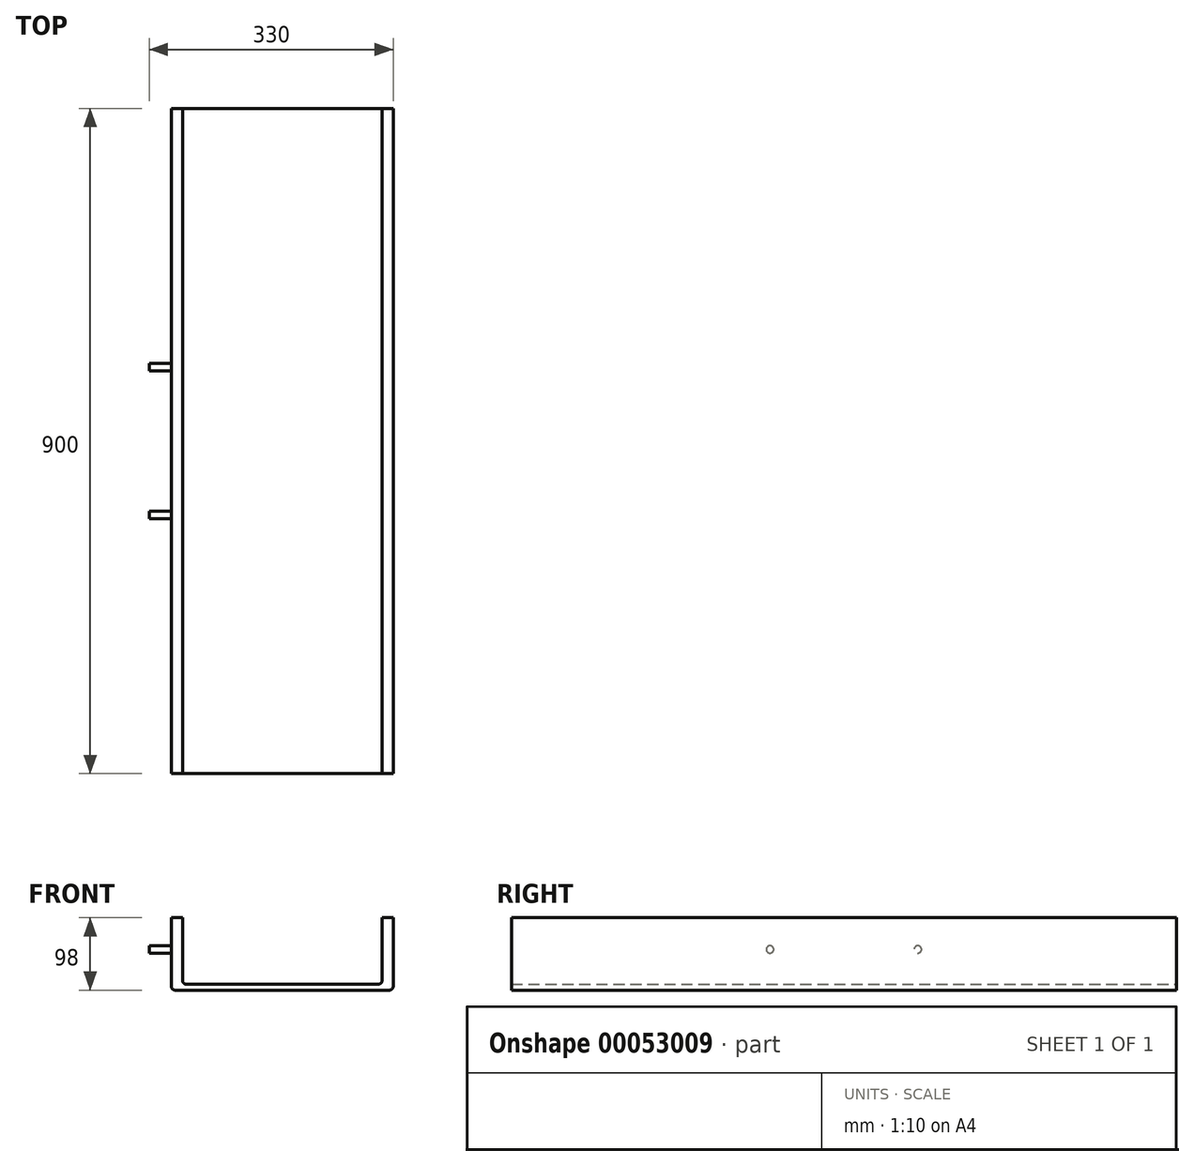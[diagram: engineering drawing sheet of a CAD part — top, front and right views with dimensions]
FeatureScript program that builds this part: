
annotation { "Feature Type Name" : "Feature", "Feature Type Description" : "" }
export const myFeature = defineFeature(function(context is Context, id is Id, definition is map)
    precondition{}
    {
        {
            var Q0;
            Q0=qCreatedBy(makeId("Front.planeOp"),FACE);
            var sketch = newSketch(context, id + "F0", { "sketchPlane" : qUnion([Q0])});
            skLineSegment(sketch, "E0", {"start": v(-280.93, 0) * mm, "end": v(9.07, 0) * mm});
            skLineSegment(sketch, "E1", {"start": v(14.07, 5) * mm, "end": v(14.07, 98) * mm});
            skLineSegment(sketch, "E2", {"start": v(14.07, 98) * mm, "end": v(-0.93, 98) * mm});
            skLineSegment(sketch, "E3", {"start": v(-0.93, 98) * mm, "end": v(-0.93, 13) * mm});
            skLineSegment(sketch, "E4", {"start": v(-5.93, 8) * mm, "end": v(-265.93, 8) * mm});
            skLineSegment(sketch, "E5", {"start": v(-270.93, 13) * mm, "end": v(-270.93, 98) * mm});
            skLineSegment(sketch, "E6", {"start": v(-270.93, 98) * mm, "end": v(-285.93, 98) * mm});
            skLineSegment(sketch, "E7", {"start": v(-285.93, 98) * mm, "end": v(-285.93, 5) * mm});
            skPoint(sketch, "E8.visualSharp", {"position": v(-270.93, 8) * mm});
            skArc(sketch, "E8.filletArc", {"start": v(-270.93, 13) * mm, "mid": v(-269.47, 9.46) * mm, "end": v(-265.93, 8) * mm});
            skPoint(sketch, "E9.visualSharp", {"position": v(-0.93, 8) * mm});
            skArc(sketch, "E9.filletArc", {"start": v(-5.93, 8) * mm, "mid": v(-2.4, 9.46) * mm, "end": v(-0.93, 13) * mm});
            skPoint(sketch, "E10.visualSharp", {"position": v(14.07, 0) * mm});
            skArc(sketch, "E10.filletArc", {"start": v(9.07, 0) * mm, "mid": v(12.6, 1.46) * mm, "end": v(14.07, 5) * mm});
            skPoint(sketch, "E11.visualSharp", {"position": v(-285.93, 0) * mm});
            skArc(sketch, "E11.filletArc", {"start": v(-285.93, 5) * mm, "mid": v(-284.47, 1.46) * mm, "end": v(-280.93, 0) * mm});
            skSolve(sketch);
        }
        {
            var Q0;
            Q0=makeQuery(id+"F0.imprint","IMPRINT",FACE,{"disambiguationData":[TD([[makeQuery(id+"F0.imprint","IMPRINT",EDGE,{"derivedFrom":sQuery(id+"F0.wireOp",EDGE,"E0")}),1.0]])]});
            extrude(context, id + "F1", {"entities" : qUnion([Q0]), "endBound" : BoundingType.SYMMETRIC, "depth" : 900 * mm});
        }
        {
            var Q0;
            Q0=makeQuery(id+"F1.opExtrude","SWEPT_FACE",FACE,{"disambiguationData":[OSD([sQuery(id+"F0.wireOp",EDGE,"E7")])]});
            var sketch = newSketch(context, id + "F2", { "sketchPlane" : qUnion([Q0])});
            skLineSegment(sketch, "E12", {"start": v(0, 0) * mm, "end": v(0, 112.52) * mm});
            skLineSegment(sketch, "E13", {"start": v(100, 55) * mm, "end": v(-100, 55) * mm});
            skCircle(sketch, "E14", {"center": v(-100, 55) * mm, "radius": 5 * mm});
            skCircle(sketch, "E15", {"center": v(100, 55) * mm, "radius": 5 * mm});
            skSolve(sketch);
        }
        {
            var Q0;
            Q0=makeQuery(id+"F2.imprint","IMPRINT",FACE,{"disambiguationData":[TD([[makeQuery(id+"F2.imprint","IMPRINT",EDGE,{"derivedFrom":sQuery(id+"F2.wireOp",EDGE,"E14")}),1.0]])]});
            var Q1;
            Q1=makeQuery(id+"F2.imprint","IMPRINT",FACE,{"disambiguationData":[TD([[makeQuery(id+"F2.imprint","IMPRINT",EDGE,{"derivedFrom":sQuery(id+"F2.wireOp",EDGE,"E15")}),1.0]])]});
            extrude(context, id + "F3", {"entities" : qUnion([Q0, Q1]), "operationType" : NewBodyOperationType.ADD, "depth" : 30 * mm});
        }
    });
